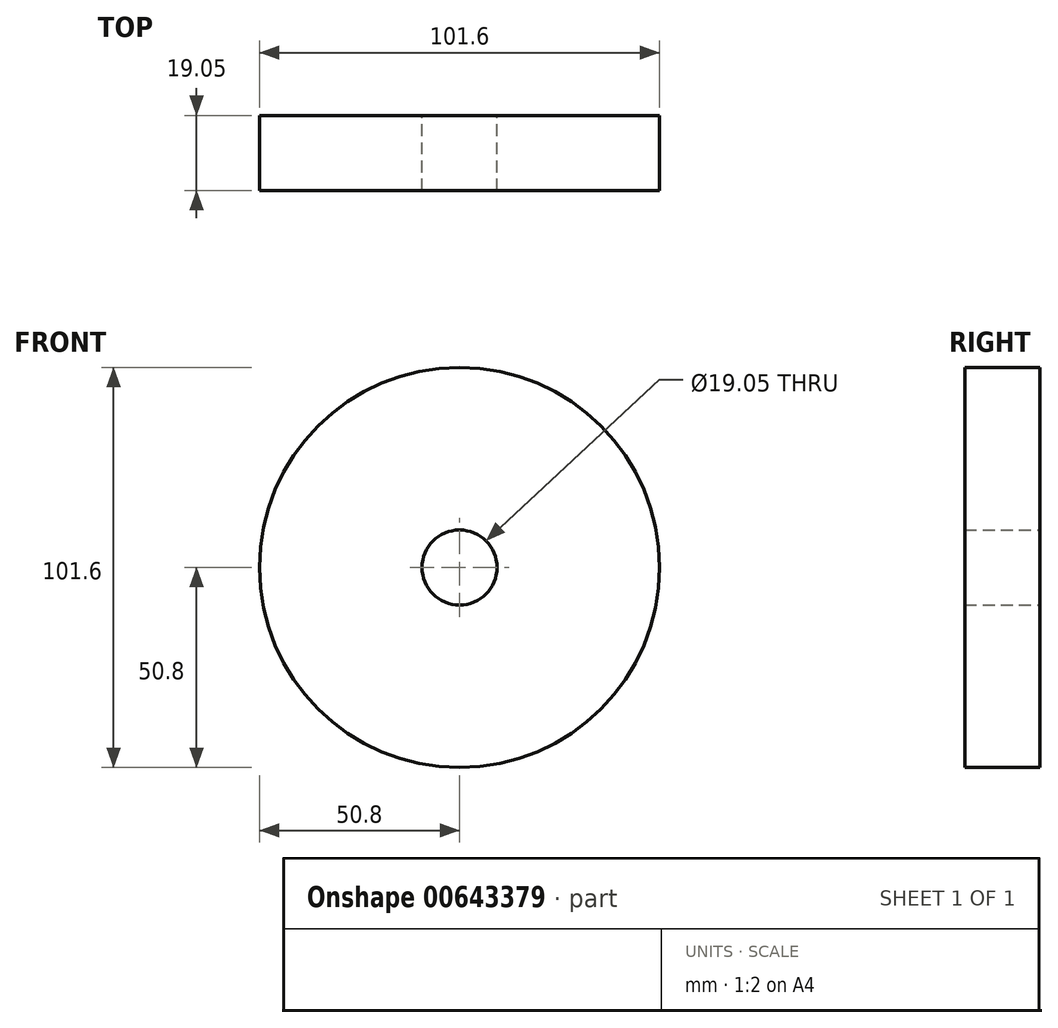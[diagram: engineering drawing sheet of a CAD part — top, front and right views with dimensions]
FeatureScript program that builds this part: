
annotation { "Feature Type Name" : "Feature", "Feature Type Description" : "" }
export const myFeature = defineFeature(function(context is Context, id is Id, definition is map)
    precondition{}
    {
        {
            var Q0;
            Q0=qCreatedBy(makeId("Front.planeOp"),FACE);
            var sketch = newSketch(context, id + "F0", { "sketchPlane" : qUnion([Q0])});
            skCircle(sketch, "E0", {"center": v(0, 0) * mm, "radius": 50.8 * mm});
            skCircle(sketch, "E1", {"center": v(0, 0) * mm, "radius": 9.53 * mm});
            skSolve(sketch);
        }
        {
            var Q0;
            Q0 = qSketchRegion(id + "F0", true);
            extrude(context, id + "F1", {"entities" : qUnion([Q0]), "depth" : 19.05 * mm, "offsetDistance" : 25.4 * mm});
        }
    });
